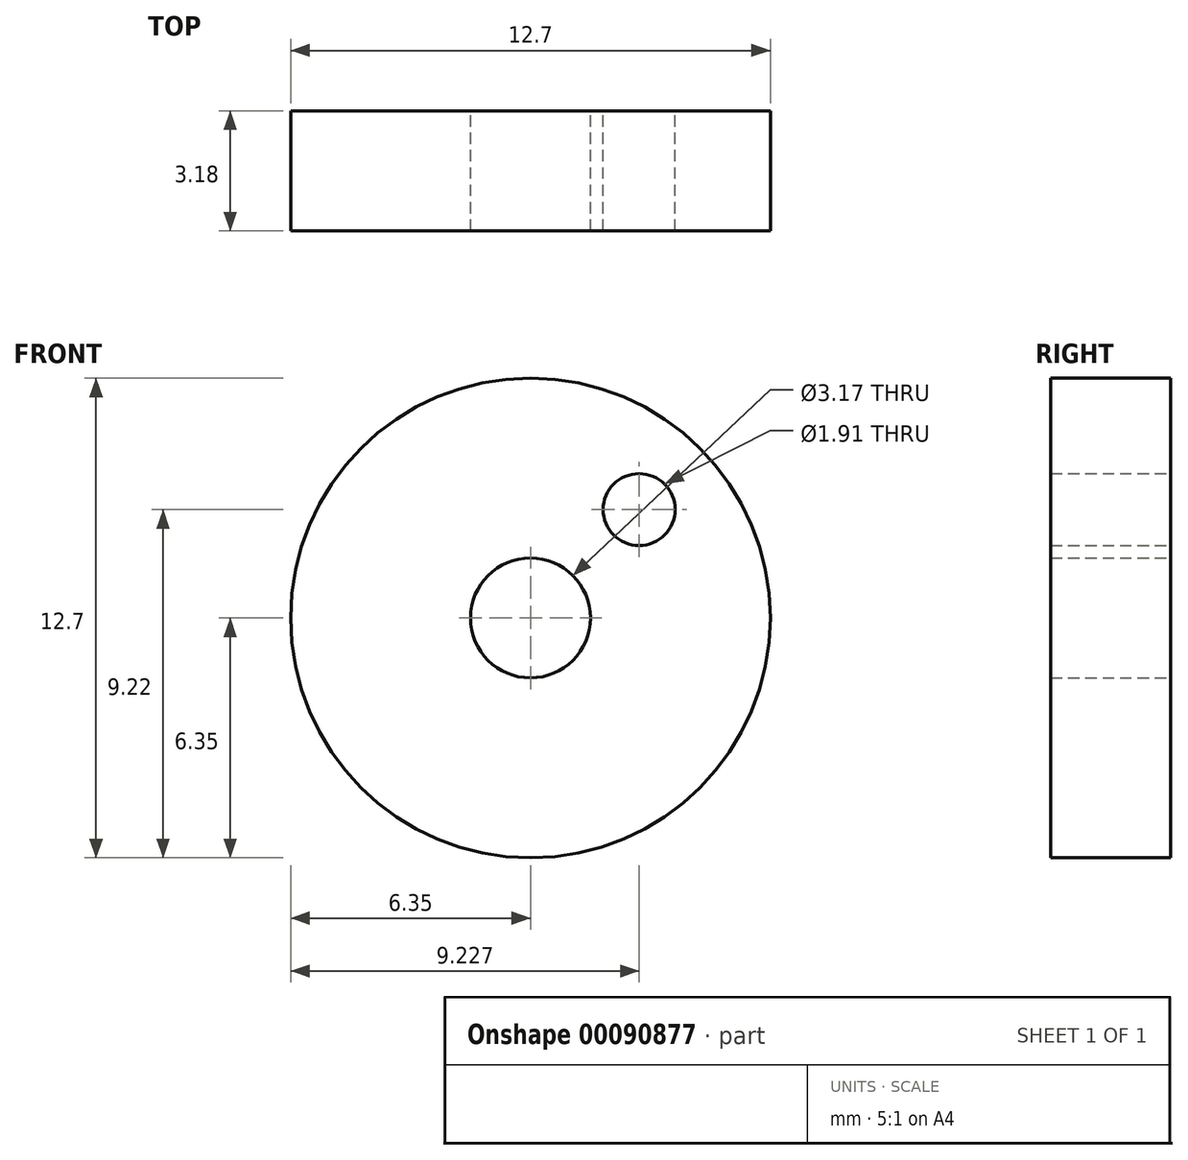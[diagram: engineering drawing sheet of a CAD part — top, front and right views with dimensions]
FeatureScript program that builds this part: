
annotation { "Feature Type Name" : "Feature", "Feature Type Description" : "" }
export const myFeature = defineFeature(function(context is Context, id is Id, definition is map)
    precondition{}
    {
        {
            var Q0;
            Q0=qCreatedBy(makeId("Front.planeOp"),FACE);
            var sketch = newSketch(context, id + "F0", { "sketchPlane" : qUnion([Q0])});
            skCircle(sketch, "E0", {"center": v(0, 0) * mm, "radius": 6.35 * mm});
            skCircle(sketch, "E1", {"center": v(0, 0) * mm, "radius": 1.59 * mm});
            skCircle(sketch, "E2", {"center": v(2.88, 2.87) * mm, "radius": 0.95 * mm});
            skSolve(sketch);
        }
        {
            var Q0;
            Q0 = qSketchRegion(id + "F0", true);
            extrude(context, id + "F1", {"entities" : qUnion([Q0]), "endBound" : BoundingType.SYMMETRIC, "depth" : 3.17 * mm});
        }
    });
